# Revit family: Crealco Shadow Cantilever
name_source: partatom
category: Generic Models
revit_build: Autodesk Revit 2016 (Build: 20150714_1515(x64)
units: mm (PartAtom-declared; Revit-internal decimal feet)

## family parameters
Always vertical = Yes
Can host rebar = No
Cut with Voids When Loaded = No
Host = Wall
Part Type = Normal
Room Calculation Point = No
Round Connector Dimension = Use Diameter
Shared = No

## types (1)
- User Defined Size
    Description = Shadow Screen
    Head Side Gap = 63 mm
    Jamb Center Side Gap = 21 mm  [stored 0.0688976 ft]
    Jamb Side Gap = 80 mm  [stored 0.262467 ft]
    Manufacturer = Crealco
    Maximum Mullion Spacing = 1800 mm  [stored 5.90551 ft]
    Middle = 37 mm
    Model = Shadow
    Mullion Top Gap = 42 mm  [stored 0.137795 ft]
    Mullion Width = 42 mm  [stored 0.137795 ft]
    Type Comments = Cantilever
    URL = https://www.crealco.co.za

note: [stored X ft] marks values corroborated as IEEE doubles in the binary element streams (Revit-internal decimal feet)

## geometry (parser evidence)
native form markers: Sweep x18
no freeform markers — native parametric forms only
